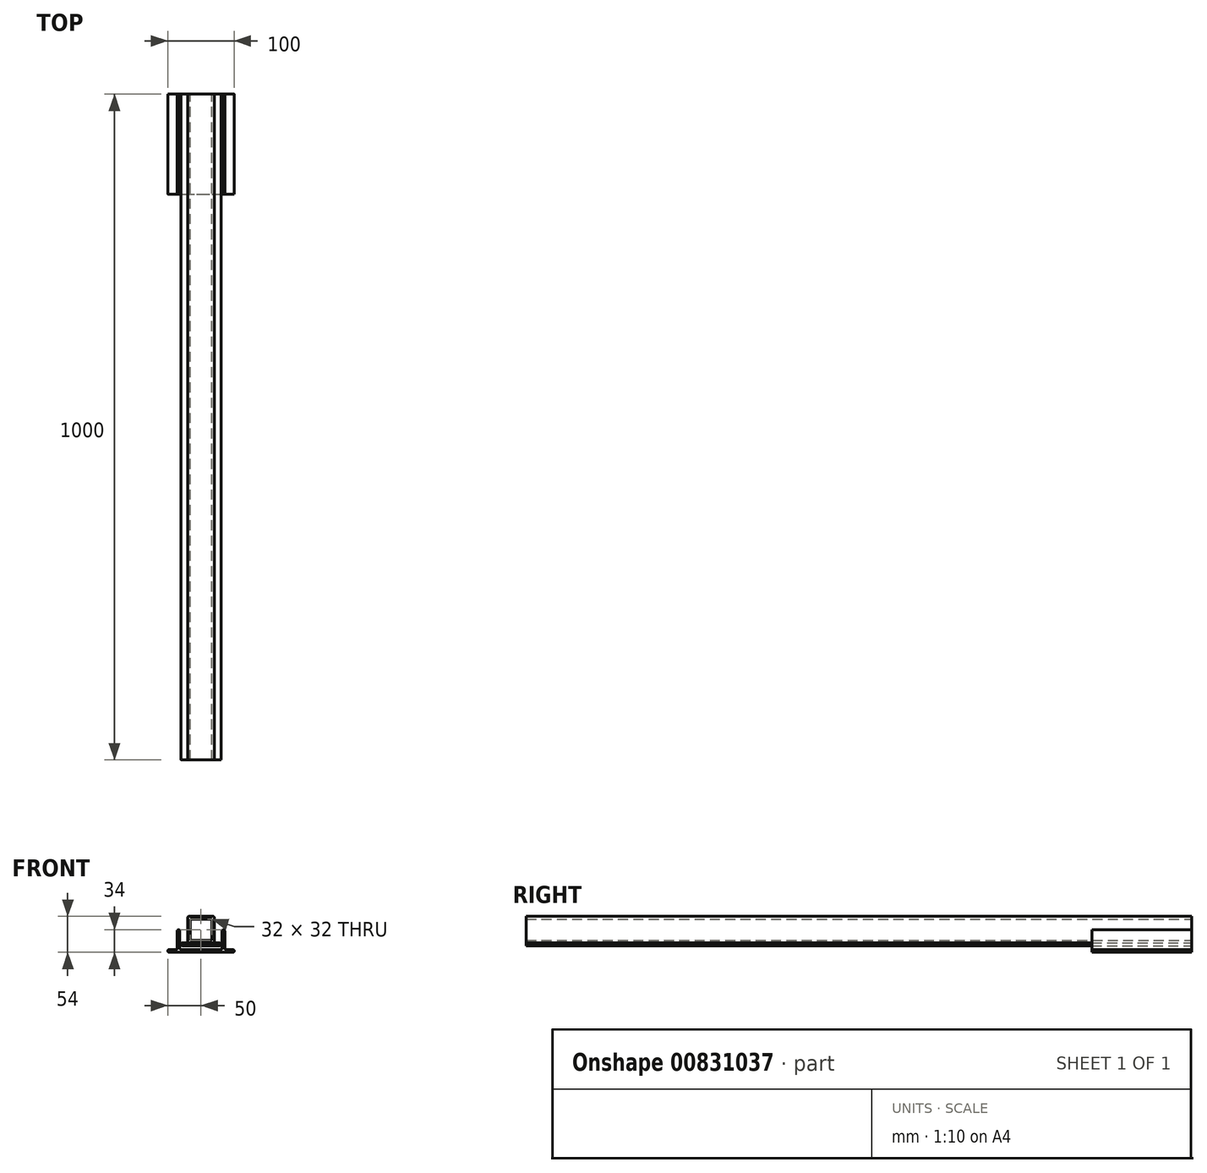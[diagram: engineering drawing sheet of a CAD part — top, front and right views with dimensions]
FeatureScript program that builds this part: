
annotation { "Feature Type Name" : "Feature", "Feature Type Description" : "" }
export const myFeature = defineFeature(function(context is Context, id is Id, definition is map)
    precondition{}
    {
        {
            var Q0;
            Q0=qCreatedBy(makeId("Front.planeOp"),FACE);
            var sketch = newSketch(context, id + "F0", { "sketchPlane" : qUnion([Q0])});
            skLineSegment(sketch, "E0.bottom", {"start": v(-28, 2) * mm, "end": v(28, 2) * mm});
            skLineSegment(sketch, "E0.top", {"start": v(-28, -2) * mm, "end": v(28, -2) * mm});
            skLineSegment(sketch, "E0.left", {"start": v(-30, 0) * mm, "end": v(-30, 0) * mm});
            skLineSegment(sketch, "E0.right", {"start": v(30, 0) * mm, "end": v(30, 0) * mm});
            skPoint(sketch, "E0.middle", {"position": v(0, 0) * mm});
            skLineSegment(sketch, "E1", {"start": v(0, 42) * mm, "end": v(0, -46.12) * mm, "construction": true});
            skPoint(sketch, "E1.endSnap0", {"position": v(0, -2) * mm});
            skLineSegment(sketch, "E2.bottom", {"start": v(-18, 42) * mm, "end": v(18, 42) * mm});
            skLineSegment(sketch, "E2.top", {"start": v(-18, 2) * mm, "end": v(18, 2) * mm});
            skLineSegment(sketch, "E2.left", {"start": v(-20, 40) * mm, "end": v(-20, 4) * mm});
            skLineSegment(sketch, "E2.right", {"start": v(20, 40) * mm, "end": v(20, 4) * mm});
            skPoint(sketch, "E3.visualSharp", {"position": v(-20, 42) * mm});
            skArc(sketch, "E3.filletArc", {"start": v(-18, 42) * mm, "mid": v(-19.41, 41.41) * mm, "end": v(-20, 40) * mm});
            skPoint(sketch, "E4.visualSharp", {"position": v(20, 42) * mm});
            skArc(sketch, "E4.filletArc", {"start": v(20, 40) * mm, "mid": v(19.41, 41.41) * mm, "end": v(18, 42) * mm});
            skPoint(sketch, "E5.visualSharp", {"position": v(-20, 2) * mm});
            skArc(sketch, "E5.filletArc", {"start": v(-20, 4) * mm, "mid": v(-19.41, 2.59) * mm, "end": v(-18, 2) * mm});
            skPoint(sketch, "E6.visualSharp", {"position": v(20, 2) * mm});
            skArc(sketch, "E6.filletArc", {"start": v(18, 2) * mm, "mid": v(19.41, 2.59) * mm, "end": v(20, 4) * mm});
            skLineSegment(sketch, "E7.0", {"start": v(-16, 38) * mm, "end": v(-16, 6) * mm});
            skLineSegment(sketch, "E7.1", {"start": v(-16, 38) * mm, "end": v(16, 38) * mm});
            skLineSegment(sketch, "E7.2", {"start": v(16, 38) * mm, "end": v(16, 6) * mm});
            skLineSegment(sketch, "E7.3", {"start": v(-16, 6) * mm, "end": v(16, 6) * mm});
            skPoint(sketch, "E8.endSnap0", {"position": v(16, 22) * mm});
            skLineSegment(sketch, "E9", {"start": v(46, 22) * mm, "end": v(-64.46, 22) * mm, "construction": true});
            skPoint(sketch, "E10.visualSharp", {"position": v(-30, 2) * mm});
            skArc(sketch, "E10.filletArc", {"start": v(-28, 2) * mm, "mid": v(-29.41, 1.41) * mm, "end": v(-30, 0) * mm});
            skPoint(sketch, "E11.visualSharp", {"position": v(-30, -2) * mm});
            skArc(sketch, "E11.filletArc", {"start": v(-30, 0) * mm, "mid": v(-29.41, -1.41) * mm, "end": v(-28, -2) * mm});
            skPoint(sketch, "E12.visualSharp", {"position": v(30, 2) * mm});
            skArc(sketch, "E12.filletArc", {"start": v(30, 0) * mm, "mid": v(29.41, 1.41) * mm, "end": v(28, 2) * mm});
            skPoint(sketch, "E13.visualSharp", {"position": v(30, -2) * mm});
            skArc(sketch, "E13.filletArc", {"start": v(28, -2) * mm, "mid": v(29.41, -1.41) * mm, "end": v(30, 0) * mm});
            skLineSegment(sketch, "E14", {"start": v(0, -8) * mm, "end": v(-29.7, -8) * mm});
            skLineSegment(sketch, "E15", {"start": v(-50, -10) * mm, "end": v(-50, -10) * mm});
            skLineSegment(sketch, "E16", {"start": v(-48, -12) * mm, "end": v(0, -12) * mm});
            skPoint(sketch, "E17.visualSharp", {"position": v(-50, -8) * mm});
            skArc(sketch, "E17.filletArc", {"start": v(-48, -8) * mm, "mid": v(-49.41, -8.59) * mm, "end": v(-50, -10) * mm});
            skPoint(sketch, "E18.visualSharp", {"position": v(-50, -12) * mm});
            skArc(sketch, "E18.filletArc", {"start": v(-50, -10) * mm, "mid": v(-49.41, -11.41) * mm, "end": v(-48, -12) * mm});
            skArc(sketch, "E19.MirrorCS", {"start": v(50, -10) * mm, "mid": v(49.41, -11.41) * mm, "end": v(48, -12) * mm});
            skArc(sketch, "E20.MirrorCS", {"start": v(48, -8) * mm, "mid": v(49.41, -8.59) * mm, "end": v(50, -10) * mm});
            skPoint(sketch, "E21.MirrorP", {"position": v(50, -12) * mm});
            skPoint(sketch, "E22.MirrorP", {"position": v(50, -8) * mm});
            skLineSegment(sketch, "E23.MirrorCS", {"start": v(0, -8) * mm, "end": v(29.7, -8) * mm});
            skLineSegment(sketch, "E24.MirrorCS", {"start": v(48, -12) * mm, "end": v(0, -12) * mm});
            skLineSegment(sketch, "E25", {"start": v(31.7, -6) * mm, "end": v(31.7, 20) * mm});
            skLineSegment(sketch, "E26", {"start": v(33.7, 22) * mm, "end": v(33.7, 22) * mm});
            skLineSegment(sketch, "E27", {"start": v(35.7, 20) * mm, "end": v(35.7, -6) * mm});
            skLineSegment(sketch, "E28.MirrorCS", {"start": v(-31.7, -6) * mm, "end": v(-31.7, 20) * mm});
            skLineSegment(sketch, "E29.MirrorCS", {"start": v(-35.7, 20) * mm, "end": v(-35.7, -6) * mm});
            skLineSegment(sketch, "E30.MirrorCS", {"start": v(-33.7, 22) * mm, "end": v(-33.7, 22) * mm});
            skLineSegment(sketch, "E31.trimOffspring", {"start": v(-37.7, -8) * mm, "end": v(-48, -8) * mm});
            skLineSegment(sketch, "E32.trimOffspring", {"start": v(37.7, -8) * mm, "end": v(48, -8) * mm});
            skPoint(sketch, "E33.visualSharp", {"position": v(35.7, -8) * mm});
            skArc(sketch, "E33.filletArc", {"start": v(35.7, -6) * mm, "mid": v(36.29, -7.41) * mm, "end": v(37.7, -8) * mm});
            skPoint(sketch, "E34.visualSharp", {"position": v(-35.7, -8) * mm});
            skArc(sketch, "E34.filletArc", {"start": v(-37.7, -8) * mm, "mid": v(-36.29, -7.41) * mm, "end": v(-35.7, -6) * mm});
            skPoint(sketch, "E35.visualSharp", {"position": v(31.7, -8) * mm});
            skArc(sketch, "E35.filletArc", {"start": v(29.7, -8) * mm, "mid": v(31.11, -7.41) * mm, "end": v(31.7, -6) * mm});
            skPoint(sketch, "E36.visualSharp", {"position": v(-31.7, -8) * mm});
            skArc(sketch, "E36.filletArc", {"start": v(-31.7, -6) * mm, "mid": v(-31.11, -7.41) * mm, "end": v(-29.7, -8) * mm});
            skPoint(sketch, "E37.visualSharp", {"position": v(-35.7, 22) * mm});
            skArc(sketch, "E37.filletArc", {"start": v(-33.7, 22) * mm, "mid": v(-35.11, 21.41) * mm, "end": v(-35.7, 20) * mm});
            skPoint(sketch, "E38.visualSharp", {"position": v(31.7, 22) * mm});
            skArc(sketch, "E38.filletArc", {"start": v(33.7, 22) * mm, "mid": v(32.29, 21.41) * mm, "end": v(31.7, 20) * mm});
            skPoint(sketch, "E39.visualSharp", {"position": v(-31.7, 22) * mm});
            skArc(sketch, "E39.filletArc", {"start": v(-31.7, 20) * mm, "mid": v(-32.29, 21.41) * mm, "end": v(-33.7, 22) * mm});
            skPoint(sketch, "E40.visualSharp", {"position": v(35.7, 22) * mm});
            skArc(sketch, "E40.filletArc", {"start": v(35.7, 20) * mm, "mid": v(35.11, 21.41) * mm, "end": v(33.7, 22) * mm});
            skLineSegment(sketch, "E41", {"start": v(47.07, 12) * mm, "end": v(-58.73, 12) * mm, "construction": true});
            skSolve(sketch);
        }
        {
            var Q0;
            Q0=makeQuery(id+"F0.imprint","IMPRINT",FACE,{"disambiguationData":[TD([[makeQuery(id+"F0.imprint","IMPRINT",EDGE,{"derivedFrom":sQuery(id+"F0.wireOp",EDGE,"E14")}),1.0]])]});
            extrude(context, id + "F1", {"entities" : qUnion([Q0]), "depth" : 150 * mm, "offsetDistance" : 25 * mm});
        }
        {
            var Q0;
            Q0=makeQuery(id+"F0.imprint","IMPRINT",FACE,{"disambiguationData":[TD([[makeQuery(id+"F0.imprint","IMPRINT",EDGE,{"derivedFrom":sQuery(id+"F0.wireOp",EDGE,"E2.bottom")}),-1.0]])]});
            extrude(context, id + "F2", {"entities" : qUnion([Q0]), "depth" : 1000 * mm, "offsetDistance" : 25 * mm});
        }
        {
            var Q0;
            Q0=makeQuery(id+"F0.imprint","IMPRINT",FACE,{"disambiguationData":[TD([[makeQuery(id+"F0.imprint","IMPRINT",EDGE,{"derivedFrom":sQuery(id+"F0.wireOp",EDGE,"E0.top")}),1.0]])]});
            extrude(context, id + "F3", {"entities" : qUnion([Q0]), "depth" : 1000 * mm, "offsetDistance" : 25 * mm});
        }
    });
